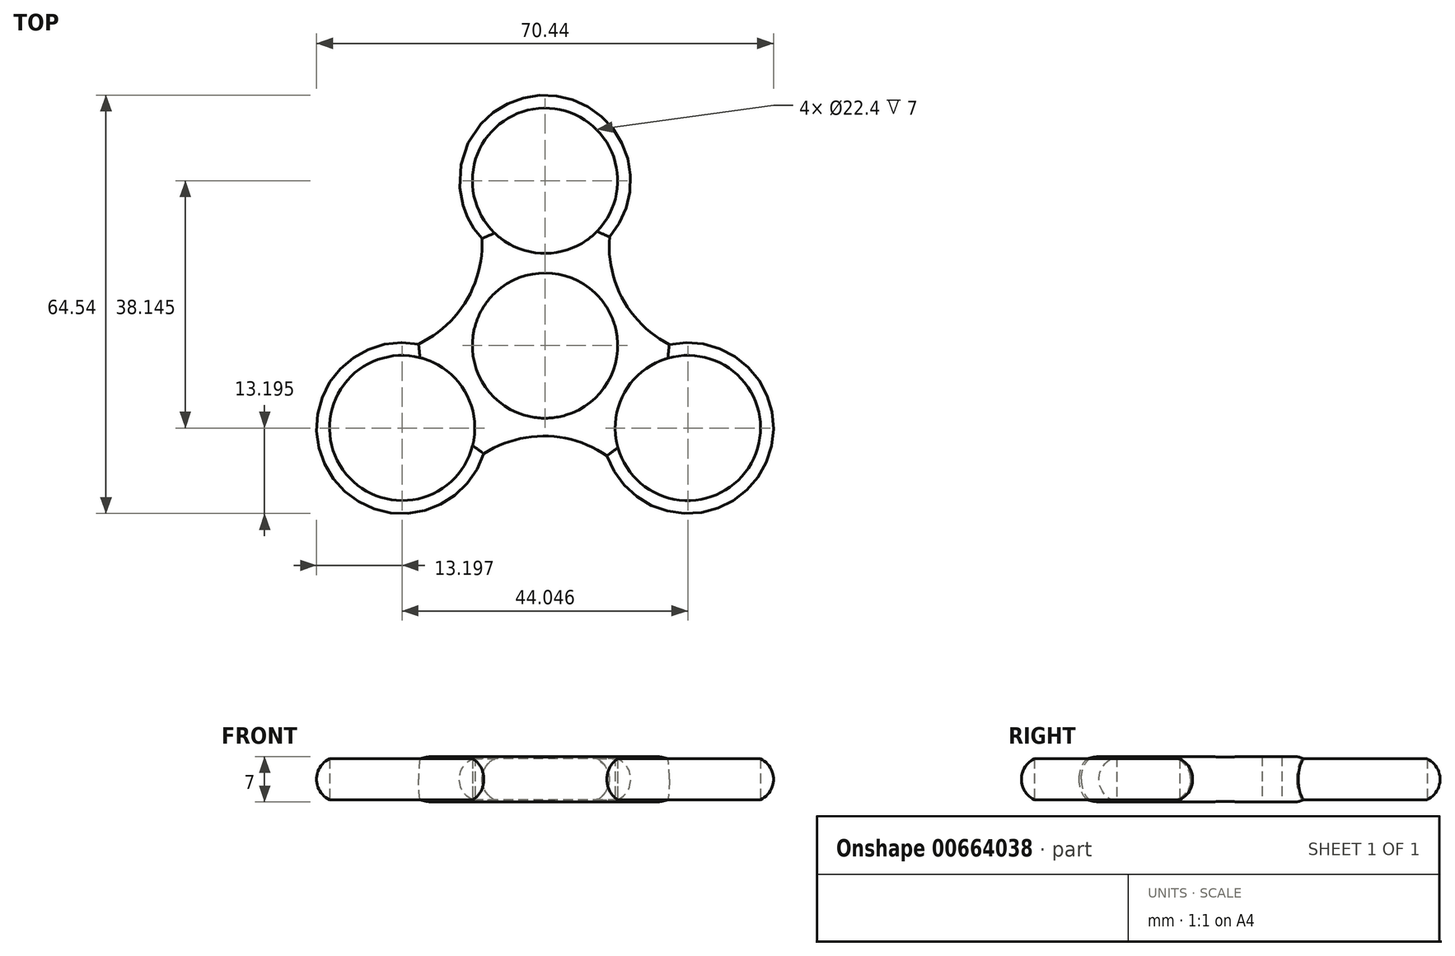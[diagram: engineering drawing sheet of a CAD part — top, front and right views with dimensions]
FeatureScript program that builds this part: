
annotation { "Feature Type Name" : "Feature", "Feature Type Description" : "" }
export const myFeature = defineFeature(function(context is Context, id is Id, definition is map)
    precondition{}
    {
        {
            var Q0;
            Q0=qCreatedBy(makeId("Top.planeOp"),FACE);
            var sketch = newSketch(context, id + "F0", { "sketchPlane" : qUnion([Q0])});
            skCircle(sketch, "E0", {"center": v(0, 0) * mm, "radius": 11.2 * mm});
            skCircle(sketch, "E1", {"center": v(0, 25.43) * mm, "radius": 11.2 * mm});
            skArc(sketch, "E2", {"start": v(9.96, 16.76) * mm, "mid": v(-0.17, 38.63) * mm, "end": v(-9.73, 16.51) * mm});
            skCircle(sketch, "E3.1.0", {"center": v(-22.02, -12.71) * mm, "radius": 11.2 * mm});
            skArc(sketch, "E3.1.1", {"start": v(-19.5, 0.24) * mm, "mid": v(-33.37, -19.46) * mm, "end": v(-9.43, -16.69) * mm});
            skCircle(sketch, "E3.2.0", {"center": v(22.02, -12.71) * mm, "radius": 11.2 * mm});
            skArc(sketch, "E3.2.1", {"start": v(9.54, -17) * mm, "mid": v(33.54, -19.17) * mm, "end": v(19.17, 0.17) * mm});
            skArc(sketch, "E4", {"start": v(9.96, 16.76) * mm, "mid": v(12.05, 7.07) * mm, "end": v(19.17, 0.17) * mm});
            skArc(sketch, "E5.1.0", {"start": v(-19.5, 0.24) * mm, "mid": v(-12.15, 6.9) * mm, "end": v(-9.73, 16.51) * mm});
            skArc(sketch, "E5.2.0", {"start": v(9.54, -17) * mm, "mid": v(0.1, -13.97) * mm, "end": v(-9.43, -16.69) * mm});
            skSolve(sketch);
        }
        {
            var Q0;
            Q0=makeQuery(id+"F0.imprint","IMPRINT",FACE,{"disambiguationData":[TD([[makeQuery(id+"F0.imprint","IMPRINT",EDGE,{"derivedFrom":sQuery(id+"F0.wireOp",EDGE,"E0")}),-1.0]])]});
            extrude(context, id + "F1", {"entities" : qUnion([Q0]), "depth" : 7 * mm, "offsetDistance" : 25 * mm});
        }
        {
            var Q0;
            Q0=makeQuery(id+"F1.opExtrude","CAP_EDGE",EDGE,{"disambiguationData":[OSD([sQuery(id+"F0.wireOp",EDGE,"E2")])],"isStart":false});
            var Q1;
            Q1=makeQuery(id+"F1.opExtrude","CAP_EDGE",EDGE,{"disambiguationData":[OSD([sQuery(id+"F0.wireOp",EDGE,"E5.1.0")])],"isStart":false});
            var Q2;
            Q2=makeQuery(id+"F1.opExtrude","CAP_EDGE",EDGE,{"disambiguationData":[OSD([sQuery(id+"F0.wireOp",EDGE,"E4")])],"isStart":false});
            var Q3;
            Q3=makeQuery(id+"F1.opExtrude","CAP_EDGE",EDGE,{"disambiguationData":[OSD([sQuery(id+"F0.wireOp",EDGE,"E3.2.1")])],"isStart":false});
            var Q4;
            Q4=makeQuery(id+"F1.opExtrude","CAP_EDGE",EDGE,{"disambiguationData":[OSD([sQuery(id+"F0.wireOp",EDGE,"E5.2.0")])],"isStart":false});
            var Q5;
            Q5=makeQuery(id+"F1.opExtrude","CAP_EDGE",EDGE,{"disambiguationData":[OSD([sQuery(id+"F0.wireOp",EDGE,"E3.1.1")])],"isStart":false});
            fillet(context, id + "F2", {"entities" : qUnion([Q0, Q1, Q2, Q3, Q4, Q5]), "radius" : 3.5 * mm, "tangentPropagation" : true, "allowEdgeOverflow" : false});
        }
        {
            var Q0;
            Q0=makeQuery(id+"F1.opExtrude","CAP_EDGE",EDGE,{"disambiguationData":[OSD([sQuery(id+"F0.wireOp",EDGE,"E3.1.1")])],"isStart":true});
            var Q1;
            Q1=makeQuery(id+"F1.opExtrude","CAP_EDGE",EDGE,{"disambiguationData":[OSD([sQuery(id+"F0.wireOp",EDGE,"E3.2.1")])],"isStart":true});
            var Q2;
            Q2=makeQuery(id+"F1.opExtrude","CAP_EDGE",EDGE,{"disambiguationData":[OSD([sQuery(id+"F0.wireOp",EDGE,"E5.2.0")])],"isStart":true});
            var Q3;
            Q3=makeQuery(id+"F1.opExtrude","CAP_EDGE",EDGE,{"disambiguationData":[OSD([sQuery(id+"F0.wireOp",EDGE,"E2")])],"isStart":true});
            var Q4;
            Q4=makeQuery(id+"F1.opExtrude","CAP_EDGE",EDGE,{"disambiguationData":[OSD([sQuery(id+"F0.wireOp",EDGE,"E4")])],"isStart":true});
            var Q5;
            Q5=makeQuery(id+"F1.opExtrude","CAP_EDGE",EDGE,{"disambiguationData":[OSD([sQuery(id+"F0.wireOp",EDGE,"E5.1.0")])],"isStart":true});
            fillet(context, id + "F3", {"entities" : qUnion([Q0, Q1, Q2, Q3, Q4, Q5]), "radius" : 3.5 * mm, "tangentPropagation" : true, "allowEdgeOverflow" : false});
        }
    });
